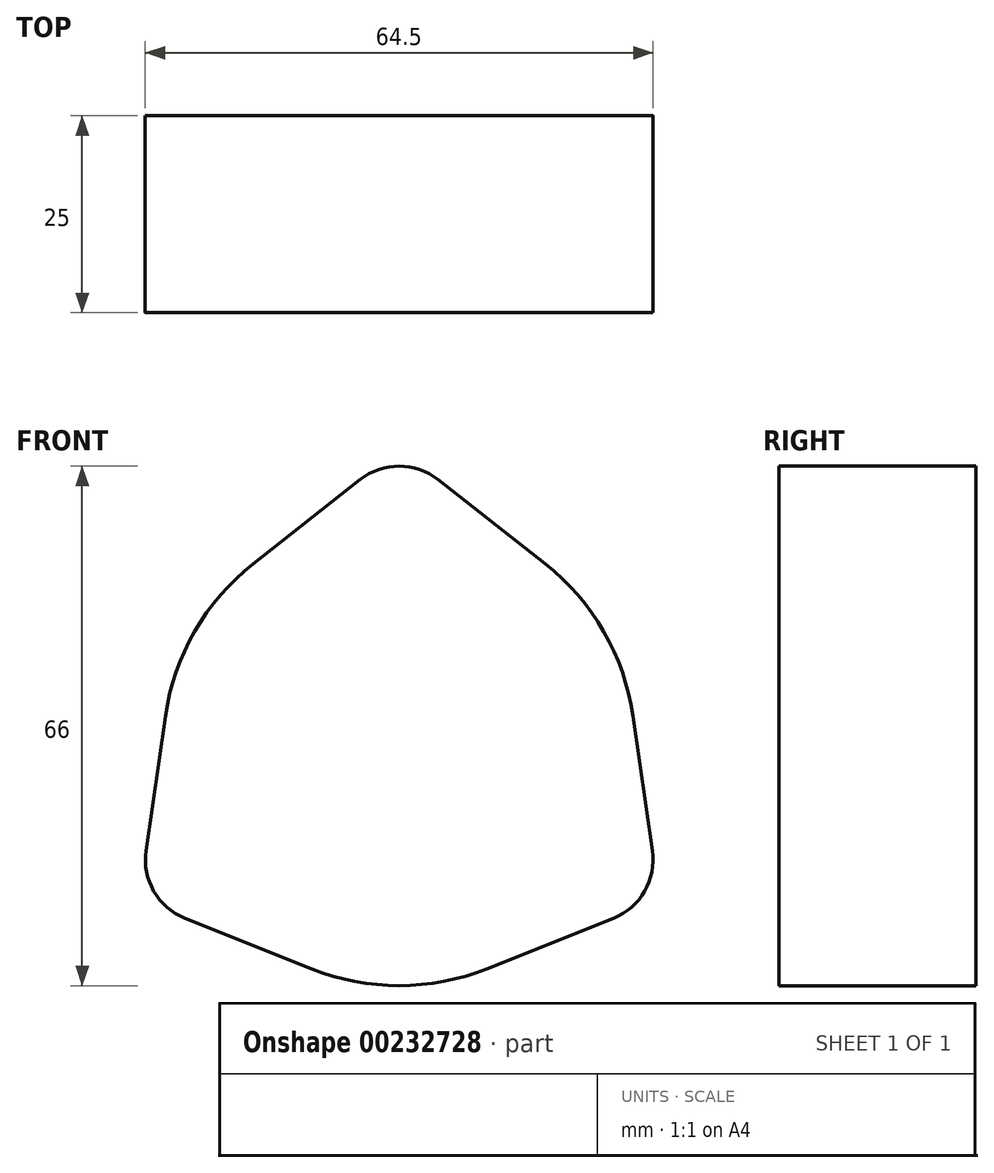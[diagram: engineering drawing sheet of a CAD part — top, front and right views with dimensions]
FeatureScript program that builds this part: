
annotation { "Feature Type Name" : "Feature", "Feature Type Description" : "" }
export const myFeature = defineFeature(function(context is Context, id is Id, definition is map)
    precondition{}
    {
        {
            var Q0;
            Q0=qCreatedBy(makeId("Front.planeOp"),FACE);
            var sketch = newSketch(context, id + "F0", { "sketchPlane" : qUnion([Q0])});
            skCircle(sketch, "E0", {"center": v(0, 0) * mm, "radius": 28 * mm});
            skArc(sketch, "E1", {"start": v(-11.13, -27.86) * mm, "mid": v(0, -30) * mm, "end": v(11.13, -27.86) * mm});
            skLineSegment(sketch, "E2", {"start": v(-4.95, 34.29) * mm, "end": v(-18.56, 23.57) * mm});
            skLineSegment(sketch, "E3", {"start": v(4.95, 34.29) * mm, "end": v(18.56, 23.57) * mm});
            skPoint(sketch, "E4.visualSharp", {"position": v(0, 38.18) * mm});
            skArc(sketch, "E4.filletArc", {"start": v(4.95, 34.29) * mm, "mid": v(0, 36) * mm, "end": v(-4.95, 34.29) * mm});
            skLineSegment(sketch, "E5.1.0", {"start": v(-27.22, -21.43) * mm, "end": v(-11.13, -27.86) * mm});
            skArc(sketch, "E5.1.1", {"start": v(-32.17, -12.86) * mm, "mid": v(-31.18, -18) * mm, "end": v(-27.22, -21.43) * mm});
            skLineSegment(sketch, "E5.1.2", {"start": v(-32.17, -12.86) * mm, "end": v(-29.7, 4.29) * mm});
            skLineSegment(sketch, "E5.2.0", {"start": v(32.17, -12.86) * mm, "end": v(29.7, 4.29) * mm});
            skArc(sketch, "E5.2.1", {"start": v(27.22, -21.43) * mm, "mid": v(31.18, -18) * mm, "end": v(32.17, -12.86) * mm});
            skLineSegment(sketch, "E5.2.2", {"start": v(27.22, -21.43) * mm, "end": v(11.13, -27.86) * mm});
            skArc(sketch, "E6.trimOffspring", {"start": v(29.7, 4.29) * mm, "mid": v(25.98, 15) * mm, "end": v(18.56, 23.57) * mm});
            skArc(sketch, "E7.trimOffspring", {"start": v(-18.56, 23.57) * mm, "mid": v(-25.98, 15) * mm, "end": v(-29.7, 4.29) * mm});
            skSolve(sketch);
        }
        {
            var Q0;
            Q0=makeQuery(id+"F0.imprint","IMPRINT",FACE,{"disambiguationData":[TD([[makeQuery(id+"F0.imprint","IMPRINT",EDGE,{"derivedFrom":sQuery(id+"F0.wireOp",EDGE,"E0")}),1.0]])]});
            var Q1;
            Q1=makeQuery(id+"F0.imprint","IMPRINT",FACE,{"disambiguationData":[TD([[makeQuery(id+"F0.imprint","IMPRINT",EDGE,{"derivedFrom":sQuery(id+"F0.wireOp",EDGE,"E0")}),-1.0]])]});
            extrude(context, id + "F1", {"entities" : qUnion([Q0, Q1]), "depth" : 25 * mm});
        }
    });
